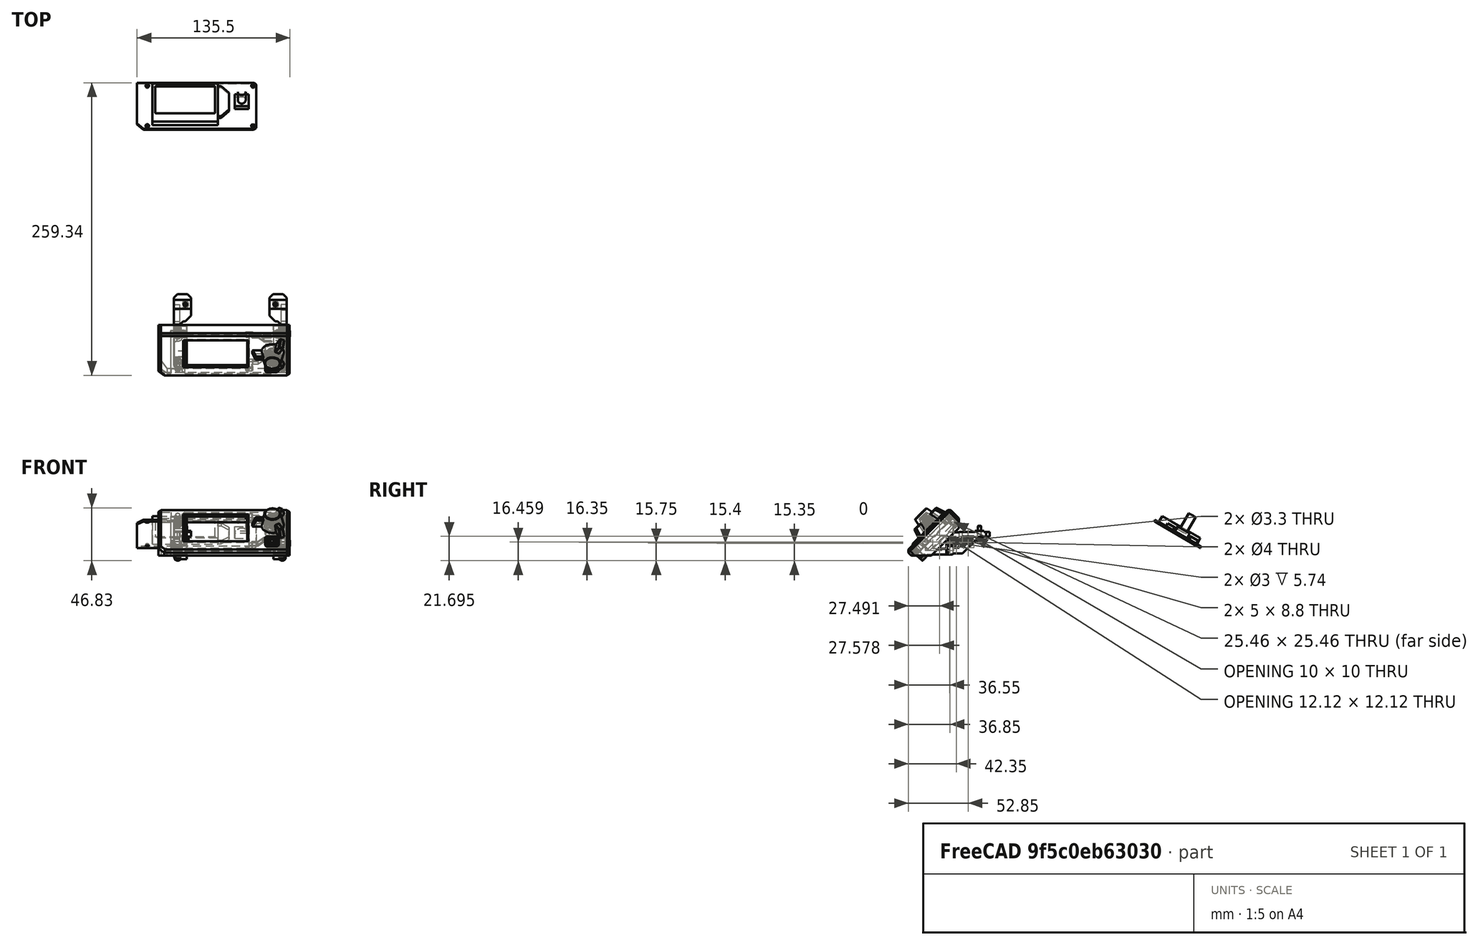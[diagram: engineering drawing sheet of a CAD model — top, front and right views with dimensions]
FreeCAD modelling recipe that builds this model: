
FCSTD DOCUMENT  (FreeCAD 0.19R24291 (Git))
Label: LCD-assembly
License: Other
LicenseURL: GPL3
objects: Part::FeaturePython×16, Part::Feature×12, App::Part×3, PartDesign::CoordinateSystem×1
note: 29 computed .brp shape members not serialized (recipe doc carries the construction recipe); baked Part::Feature solids carry a one-line shape summary decoded from their .brp

FEATURE [Part::Feature] Part__Mirroring002003004  label="mount-arm-right"
  Placement = pos=(131.75,0,0) rot=(0,0,1;0rad)
  shape: bbox 11 x 36.77 x 36.77 mm, 36 faces (baked)
FEATURE [Part::Feature] Chamfer016011001  label="mount-arm-left"
  Placement = pos=(33,-165.5,-10.25) rot=(0,0,1;3.14159rad)
  shape: bbox 11 x 36.77 x 36.77 mm, 36 faces (baked)
FEATURE [Part::Feature] Cut004005004003002008001008001001  label="lcd-base"
  Placement = pos=(84,113,-24.25) rot=(0,0,1;0rad)
  shape: bbox 116 x 44.52 x 40.02 mm, 83 faces (baked)
FEATURE [Part::Feature] Fusion001001001  label="knob"
  Placement = pos=(120,-187.5,20) rot=(0,0,1;0rad)
  shape: bbox 28.26 x 26.66 x 26.66 mm, 135 faces (baked)
FEATURE [Part::Feature] Fusion003007008004003002005002002002003002001001  label="reset-button"
  Placement = pos=(104.5,-202,0) rot=(0,0,1;0rad)
  shape: bbox 12 x 9.369 x 10.08 mm, 51 faces (baked)
FEATURE [Part::Feature] Chamfer004001001  label="lcd-mounter-right"
  Placement = pos=(127.5,-165.2,-10.3) rot=(0,0,1;3.14159rad)
  shape: bbox 15 x 38 x 21 mm, 33 faces (baked)
FEATURE [Part::Feature] Part__Mirroring002003005  label="lcd-mounter-left"
  Placement = pos=(165.2,0,0) rot=(0,0,1;0rad)
  shape: bbox 15 x 38 x 21 mm, 33 faces (baked)
FEATURE [Part::Feature] Chamfer016038001  label="led-cover_use_dark_color_filament"
  Placement = pos=(100.3,-193.677,2.05061) rot=(1,0,0;0.785398rad)
  shape: bbox 36 x 34.72 x 34.72 mm, 62 faces (baked)
FEATURE [Part::FeaturePython] Screw  label="M3x10-Screw"  # Fasteners workbench fastener (typed FeaturePython)
  Placement = pos=(32.7,-171.2,3.7) rot=(0,-1,0;1.5708rad)
  baseObject = -> Part__Mirroring002003005 [Edge92]
  diameter = 4
  invert = true
  length = 3
  lengthCustom = 10
  matchOuter = true
  offset = 0
  thread = false
  type = 33
FEATURE [Part::FeaturePython] Screw001  label="M3x10-Screw004"  # Fasteners workbench fastener (typed FeaturePython)
  Placement = pos=(132.5,-171.2,3.7) rot=(0,1,0;1.5708rad)
  baseObject = -> Chamfer004001001 [Edge92]
  diameter = 4
  invert = false
  length = 3
  lengthCustom = 10
  matchOuter = true
  offset = 0
  thread = false
  type = 33
FEATURE [Part::FeaturePython] Screw002  label="M3x8-Screw"  # Fasteners workbench fastener (typed FeaturePython)
  Placement = pos=(36,-166.914,21.2816) rot=(1,0,0;3.92699rad)
  baseObject = -> Chamfer016011001 [Edge66]
  diameter = 4
  invert = false
  length = 2
  lengthCustom = 8
  matchOuter = true
  offset = 0
  thread = false
  type = 34
FEATURE [Part::FeaturePython] Screw003  label="M3x8-Screw001"  # Fasteners workbench fastener (typed FeaturePython)
  Placement = pos=(36,-195.906,-7.70981) rot=(1,0,0;3.92699rad)
  baseObject = -> Chamfer016011001 [Edge18]
  diameter = 4
  invert = false
  length = 2
  lengthCustom = 8
  matchOuter = true
  offset = 0
  thread = false
  type = 34
FEATURE [Part::FeaturePython] Screw004  label="M3x8-Screw002"  # Fasteners workbench fastener (typed FeaturePython)
  Placement = pos=(128.75,-166.914,21.2816) rot=(1,0,0;3.92699rad)
  baseObject = -> Part__Mirroring002003004 [Edge66]
  diameter = 4
  invert = true
  length = 2
  lengthCustom = 8
  matchOuter = true
  offset = 0
  thread = false
  type = 34
FEATURE [Part::FeaturePython] Screw005  label="M3x8-Screw003"  # Fasteners workbench fastener (typed FeaturePython)
  Placement = pos=(128.75,-195.906,-7.70981) rot=(1,0,0;3.92699rad)
  baseObject = -> Part__Mirroring002003004 [Edge18]
  diameter = 4
  invert = true
  length = 2
  lengthCustom = 8
  matchOuter = true
  offset = 0
  thread = false
  type = 34
FEATURE [Part::FeaturePython] Washer  label="M3-Washer"  # Fasteners workbench fastener (typed FeaturePython)
  Placement = pos=(122.5,-145.2,9.7) rot=(1,0,0;3.14159rad)
  baseObject = -> Chamfer004001001 [Edge15]
  diameter = 4
  invert = true
  matchOuter = true
  offset = 0
  type = 5
FEATURE [Part::FeaturePython] Washer001  label="M3-Washer001"  # Fasteners workbench fastener (typed FeaturePython)
  Placement = pos=(42.7,-145.2,9.7) rot=(1,0,0;3.14159rad)
  baseObject = -> Part__Mirroring002003005 [Edge15]
  diameter = 4
  invert = false
  matchOuter = true
  offset = 0
  type = 5
FEATURE [Part::FeaturePython] Screw006  label="M3x10-Screw002"  # Fasteners workbench fastener (typed FeaturePython)
  Placement = pos=(122.5,-145.2,9.15) rot=(1,0,0;3.14159rad)
  baseObject = -> Washer [Edge1]
  diameter = 4
  invert = false
  length = 3
  lengthCustom = 10
  matchOuter = true
  offset = 0
  thread = false
  type = 34
FEATURE [Part::FeaturePython] Screw007  label="M3x10-Screw003"  # Fasteners workbench fastener (typed FeaturePython)
  Placement = pos=(42.7,-145.2,9.15) rot=(1,0,0;3.14159rad)
  baseObject = -> Washer001 [Edge1]
  diameter = 4
  invert = false
  length = 3
  lengthCustom = 10
  matchOuter = true
  offset = 0
  thread = false
  type = 34
FEATURE [Part::FeaturePython] HeatSet  label="M3x4-HeatSet"  # WARN: FeaturePython — macro-defined, semantics opaque (R4)
  Placement = pos=(120.75,-171.5,3.75) rot=(0,-1,0;1.5708rad)
  baseObject = -> Part__Mirroring002003004 [Edge77]
  diameter = 3
  invert = true
  offset = 0
FEATURE [Part::FeaturePython] HeatSet001  label="M3x4-HeatSet001"  # WARN: FeaturePython — macro-defined, semantics opaque (R4)
  Placement = pos=(44,-171.5,3.75) rot=(0,1,0;1.5708rad)
  baseObject = -> Chamfer016011001 [Edge77]
  diameter = 3
  invert = false
  offset = 0
FEATURE [Part::FeaturePython] HeatSet002  label="M3x4-HeatSet002"  # WARN: FeaturePython — macro-defined, semantics opaque (R4)
  Placement = pos=(129,-170.572,24.5404) rot=(1,0,0;3.92699rad)
  baseObject = -> Cut004005004003002008001008001001 [Edge201]
  diameter = 3
  invert = true
  offset = 0
FEATURE [Part::FeaturePython] HeatSet003  label="M3x4-HeatSet003"  # WARN: FeaturePython — macro-defined, semantics opaque (R4)
  Placement = pos=(129,-199.564,-4.45101) rot=(1,0,0;3.92699rad)
  baseObject = -> Cut004005004003002008001008001001 [Edge203]
  diameter = 3
  invert = true
  offset = 0
FEATURE [Part::FeaturePython] HeatSet004  label="M3x4-HeatSet004"  # WARN: FeaturePython — macro-defined, semantics opaque (R4)
  Placement = pos=(36,-170.572,24.5404) rot=(1,0,0;3.92699rad)
  baseObject = -> Cut004005004003002008001008001001 [Edge199]
  diameter = 3
  invert = true
  offset = 0
FEATURE [Part::FeaturePython] HeatSet005  label="M3x4-HeatSet005"  # WARN: FeaturePython — macro-defined, semantics opaque (R4)
  Placement = pos=(36,-199.564,-4.45101) rot=(1,0,0;3.92699rad)
  baseObject = -> Cut004005004003002008001008001001 [Edge200]
  diameter = 3
  invert = true
  offset = 0
FEATURE [Part::Feature] Part__Feature1667  label="Mini12864 Screen v1"
  shape: bbox 105.8 x 41.5 x 24.89 mm, 13 faces (baked)
FEATURE [Part::Feature] Part__Feature1672  label="Mini12864 Screen v006"
  shape: bbox 10 x 28.35 x 18.1 mm, 8 faces (baked)
FEATURE [Part::Feature] Part__Feature1668  label="Mini12864 Screen v002"
  shape: bbox 58 x 36.77 x 24.7 mm, 15 faces (baked)
FEATURE [Part::Feature] Part__Feature1669  label="Mini12864 Screen v003"
  shape: bbox 12.25 x 18.34 x 22.13 mm, 8 faces (baked)
FEATURE [App::Part] Mini12864_Screen_v1  label="Mini12864-LCD"
  Group = -> [Part__Feature1667,Part__Feature1668,Part__Feature1669,Part__Feature1672]
  Origin = -> Origin328
FEATURE [App::Part] Mini12864_Screen_v1001  label="Mini12864"
  Group = -> [Mini12864_Screen_v1]
  Origin = -> Origin329
  Placement = pos=(26.975,-181.529,-21.9846) rot=(1,0,0;1.309rad)
FEATURE [PartDesign::CoordinateSystem] LCS_LCD
  AttacherType = Attacher::AttachEngine3D
FEATURE [App::Part] Part  label="LCD-retro"
  Group = -> [Part__Mirroring002003004,Chamfer016011001,Cut004005004003002008001008001001,Fusion001001001,Fusion003007008004003002005002002002003002001001,Chamfer004001001,Part__Mirroring002003005,Chamfer016038001,Screw,Screw001,Screw002,Screw003,Screw004,Screw005,Washer,Washer001,Screw006,Screw007,HeatSet,HeatSet001,HeatSet002,HeatSet003,HeatSet004,HeatSet005,Mini12864_Screen_v1001,LCS_LCD]
  Origin = -> Origin
